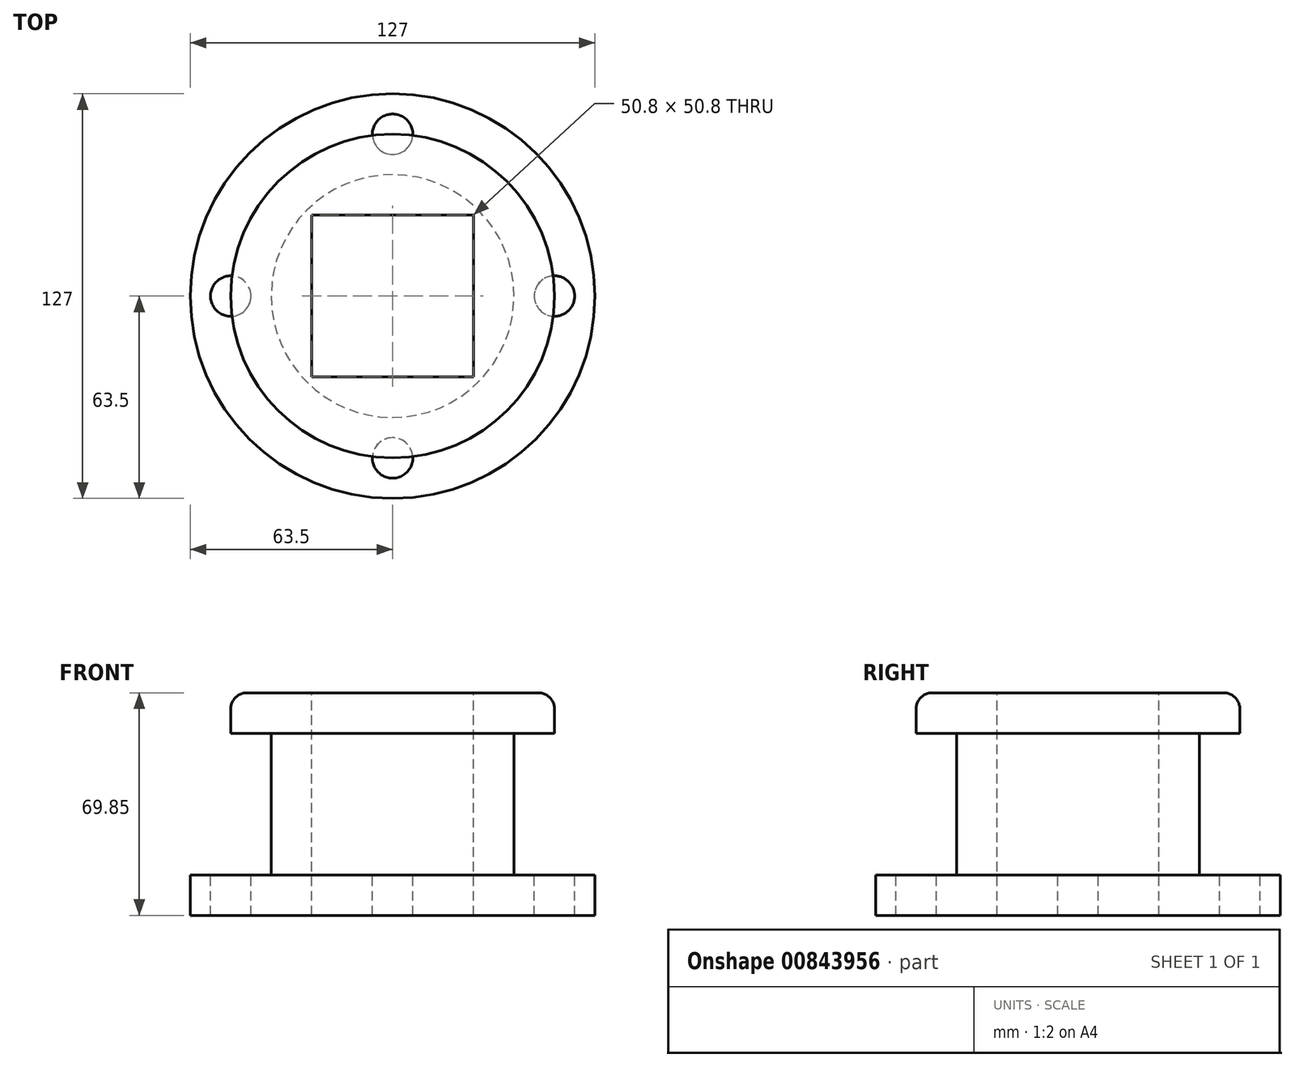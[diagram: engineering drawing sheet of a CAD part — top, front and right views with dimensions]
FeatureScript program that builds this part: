
annotation { "Feature Type Name" : "Feature", "Feature Type Description" : "" }
export const myFeature = defineFeature(function(context is Context, id is Id, definition is map)
    precondition{}
    {
        {
            var Q0;
            Q0=qCreatedBy(makeId("Top.planeOp"),FACE);
            var sketch = newSketch(context, id + "F0", { "sketchPlane" : qUnion([Q0])});
            skCircle(sketch, "E0", {"center": v(0, 0) * mm, "radius": 38.1 * mm});
            skSolve(sketch);
        }
        {
            var Q0;
            Q0 = qSketchRegion(id + "F0", true);
            extrude(context, id + "F1", {"entities" : qUnion([Q0]), "depth" : 57.15 * mm, "offsetDistance" : 25.4 * mm});
        }
        {
            var Q0;
            Q0=qCreatedBy(makeId("Top.planeOp"),FACE);
            var sketch = newSketch(context, id + "F2", { "sketchPlane" : qUnion([Q0])});
            skCircle(sketch, "E1", {"center": v(0, 0) * mm, "radius": 63.5 * mm});
            skSolve(sketch);
        }
        {
            var Q0;
            Q0 = qSketchRegion(id + "F2", true);
            extrude(context, id + "F3", {"entities" : qUnion([Q0]), "operationType" : NewBodyOperationType.ADD, "depth" : 12.7 * mm, "offsetDistance" : 25.4 * mm});
        }
        {
            var Q0;
            Q0=makeQuery(id+"F1.opExtrude","CAP_FACE",FACE,{"disambiguationData":[OSD([sQuery(id+"F0.wireOp",EDGE,"E0")])],"isStart":false});
            var sketch = newSketch(context, id + "F4", { "sketchPlane" : qUnion([Q0])});
            skCircle(sketch, "E2", {"center": v(0, 0) * mm, "radius": 50.8 * mm});
            skSolve(sketch);
        }
        {
            var Q0;
            Q0 = qSketchRegion(id + "F4", true);
            extrude(context, id + "F5", {"entities" : qUnion([Q0]), "operationType" : NewBodyOperationType.ADD, "depth" : 12.7 * mm, "offsetDistance" : 25.4 * mm});
        }
        {
            var Q0;
            Q0=makeQuery(id+"F5.opExtrude","CAP_FACE",FACE,{"disambiguationData":[OSD([sQuery(id+"F4.wireOp",EDGE,"E2")])],"isStart":false});
            var sketch = newSketch(context, id + "F6", { "sketchPlane" : qUnion([Q0])});
            skLineSegment(sketch, "E3.bottom", {"start": v(25.4, 25.4) * mm, "end": v(-25.4, 25.4) * mm});
            skLineSegment(sketch, "E3.top", {"start": v(25.4, -25.4) * mm, "end": v(-25.4, -25.4) * mm});
            skLineSegment(sketch, "E3.left", {"start": v(25.4, 25.4) * mm, "end": v(25.4, -25.4) * mm});
            skLineSegment(sketch, "E3.right", {"start": v(-25.4, 25.4) * mm, "end": v(-25.4, -25.4) * mm});
            skPoint(sketch, "E3.middle", {"position": v(0, 0) * mm});
            skSolve(sketch);
        }
        {
            var Q0;
            Q0=makeQuery(id+"F6.imprint","IMPRINT",FACE,{"disambiguationData":[TD([[makeQuery(id+"F6.imprint","IMPRINT",EDGE,{"derivedFrom":sQuery(id+"F6.wireOp",EDGE,"E3.bottom")}),1.0]])]});
            extrude(context, id + "F7", {"entities" : qUnion([Q0]), "operationType" : NewBodyOperationType.REMOVE, "oppositeDirection" : true, "depth" : 76.2 * mm, "offsetDistance" : 25.4 * mm});
        }
        {
            var Q0;
            Q0=makeQuery(id+"F5.opExtrude","CAP_EDGE",EDGE,{"disambiguationData":[OSD([sQuery(id+"F4.wireOp",EDGE,"E2")])],"isStart":false});
            fillet(context, id + "F8", {"entities" : qUnion([Q0]), "radius" : 5.08 * mm, "tangentPropagation" : true, "allowEdgeOverflow" : false});
        }
        {
            var Q0;
            Q0=makeQuery(id+"F3.opExtrude","CAP_FACE",FACE,{"disambiguationData":[OSD([sQuery(id+"F2.wireOp",EDGE,"E1")])],"isStart":false});
            var sketch = newSketch(context, id + "F9", { "sketchPlane" : qUnion([Q0])});
            skCircle(sketch, "E4", {"center": v(0, 50.8) * mm, "radius": 6.35 * mm});
            skCircle(sketch, "E5", {"center": v(50.8, 0) * mm, "radius": 6.35 * mm});
            skCircle(sketch, "E6.MirrorC", {"center": v(0, -50.8) * mm, "radius": 6.35 * mm});
            skCircle(sketch, "E7.MirrorC", {"center": v(-50.8, 0) * mm, "radius": 6.35 * mm});
            skSolve(sketch);
        }
        {
            var Q0;
            Q0 = qSketchRegion(id + "F9", true);
            extrude(context, id + "F10", {"entities" : qUnion([Q0]), "operationType" : NewBodyOperationType.REMOVE, "oppositeDirection" : true, "depth" : 25.4 * mm, "offsetDistance" : 25.4 * mm});
        }
    });
